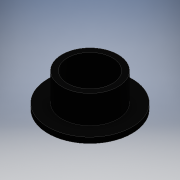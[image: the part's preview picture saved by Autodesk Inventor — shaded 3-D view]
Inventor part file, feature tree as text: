
AUTODESK INVENTOR PART (.ipt)
format: ipt  version: 2020.2 (Build 242310000, 310)  size: 103,424 bytes
history: native  units: mm
features: extrude x2, other x1, sketch x1
ambient origin geometry x8: Origin, YZ Plane, XZ Plane, XY Plane, X Axis, Y Axis, Z Axis, Center Point
bodies: Body1 (feature_tree)
feature tree (4):
  other  "ソリッド1"
  sketch  "スケッチ1"
  extrude  "押し出し1"  Depth=15.0mm
  extrude  "押し出し2"  Depth=10.0mm
